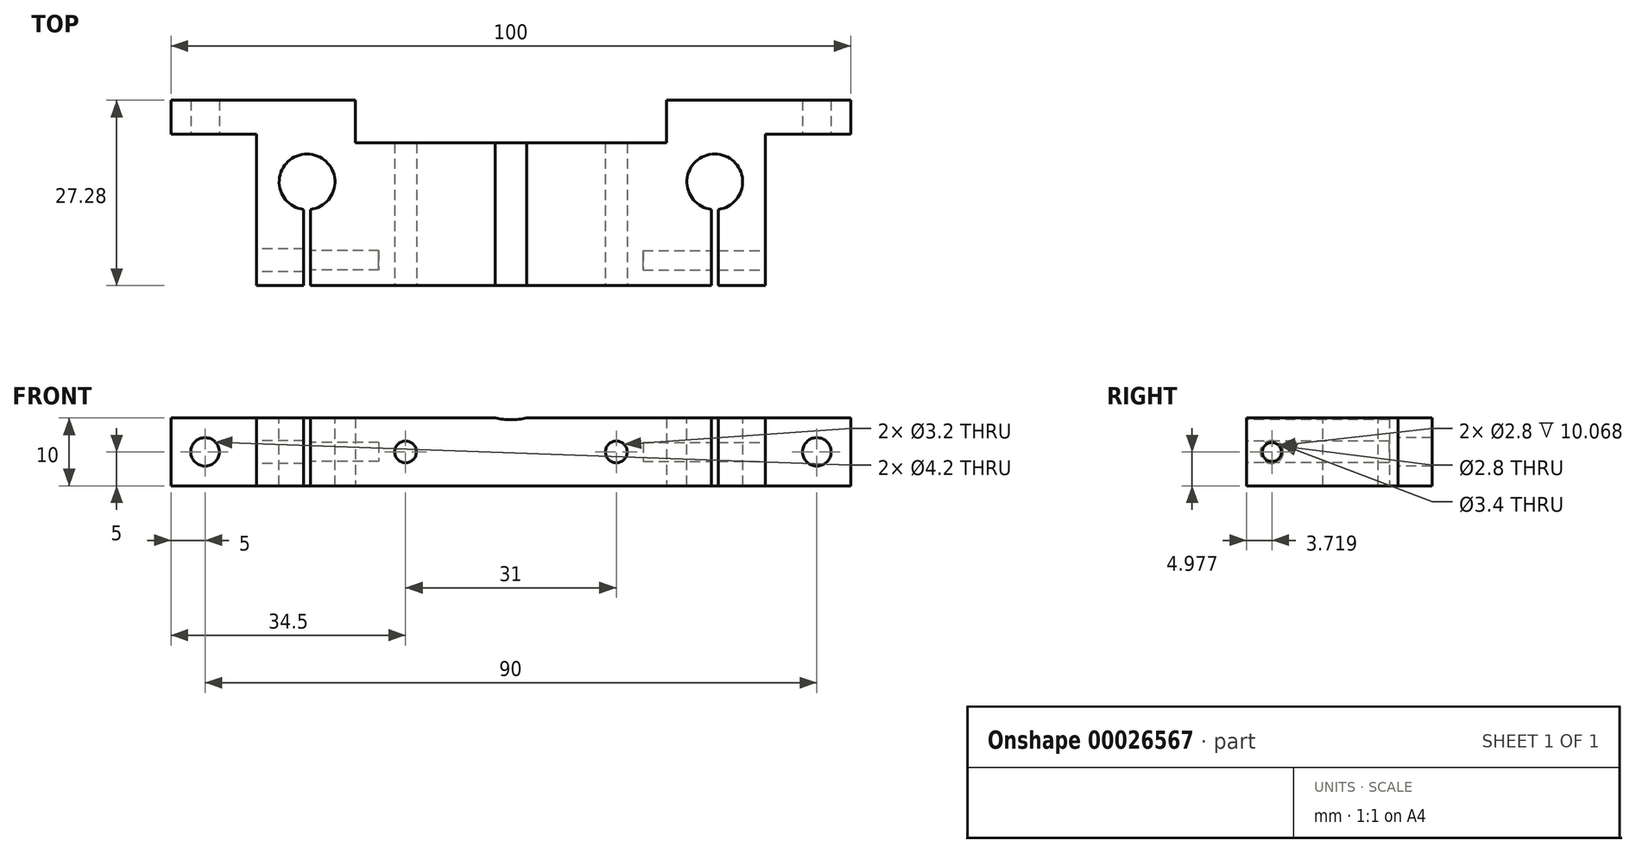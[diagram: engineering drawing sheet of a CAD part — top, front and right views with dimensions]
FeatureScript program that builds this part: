
annotation { "Feature Type Name" : "Feature", "Feature Type Description" : "" }
export const myFeature = defineFeature(function(context is Context, id is Id, definition is map)
    precondition{}
    {
        {
            var Q0;
            Q0=qCreatedBy(makeId("Top.planeOp"),FACE);
            var sketch = newSketch(context, id + "F0", { "sketchPlane" : qUnion([Q0])});
            skLineSegment(sketch, "E0", {"start": v(0, -13.82) * mm, "end": v(-37.44, -13.82) * mm});
            skLineSegment(sketch, "E1", {"start": v(-37.44, -13.82) * mm, "end": v(-37.44, 8.46) * mm});
            skLineSegment(sketch, "E2", {"start": v(-37.44, 8.46) * mm, "end": v(-50, 8.46) * mm});
            skLineSegment(sketch, "E3", {"start": v(-50, 8.46) * mm, "end": v(-50, 13.46) * mm});
            skLineSegment(sketch, "E4", {"start": v(-50, 13.46) * mm, "end": v(-22.87, 13.46) * mm});
            skLineSegment(sketch, "E5", {"start": v(-22.87, 13.46) * mm, "end": v(-22.87, 7.18) * mm});
            skLineSegment(sketch, "E6", {"start": v(-22.87, 7.18) * mm, "end": v(0, 7.18) * mm});
            skLineSegment(sketch, "E7", {"start": v(0, 7.18) * mm, "end": v(0, -13.82) * mm});
            skSolve(sketch);
        }
        {
            var Q0;
            Q0=qSketchRegion(id+"F0",true);
            extrude(context, id + "F1", {"entities" : qUnion([Q0]), "depth" : 10 * mm});
        }
        {
            var Q0;
            Q0=makeQuery(id+"F1.opExtrude","SWEPT_FACE",FACE,{"disambiguationData":[OSD([sQuery(id+"F0.wireOp",EDGE,"E0")])]});
            var sketch = newSketch(context, id + "F2", { "sketchPlane" : qUnion([Q0])});
            skLineSegment(sketch, "E8", {"start": v(0, 5) * mm, "end": v(0, 5) * mm});
            skCircle(sketch, "E9", {"center": v(-15.5, 5) * mm, "radius": 1.6 * mm});
            skCircle(sketch, "E10", {"center": v(0, 20.5) * mm, "radius": 10.75 * mm});
            skSolve(sketch);
        }
        {
            var Q0;
            Q0=qSketchRegion(id+"F2",true);
            extrude(context, id + "F3", {"entities" : qUnion([Q0]), "operationType" : NewBodyOperationType.REMOVE, "endBound" : BoundingType.THROUGH_ALL, "oppositeDirection" : true, "depth" : 25 * mm});
        }
        {
            var Q0;
            Q0=makeQuery(id+"F1.opExtrude","SWEPT_FACE",FACE,{"disambiguationData":[OSD([sQuery(id+"F0.wireOp",EDGE,"E2")])]});
            var sketch = newSketch(context, id + "F4", { "sketchPlane" : qUnion([Q0])});
            skLineSegment(sketch, "E11", {"start": v(-50, 5) * mm, "end": v(-37.44, 5) * mm, "construction": true});
            skLineSegment(sketch, "E12", {"start": v(-43.72, 10) * mm, "end": v(-43.72, 0) * mm, "construction": true});
            skCircle(sketch, "E13", {"center": v(-45, 5) * mm, "radius": 2.1 * mm});
            skSolve(sketch);
        }
        {
            var Q0;
            Q0=qSketchRegion(id+"F4",true);
            extrude(context, id + "F5", {"entities" : qUnion([Q0]), "operationType" : NewBodyOperationType.REMOVE, "endBound" : BoundingType.THROUGH_ALL, "oppositeDirection" : true, "depth" : 25 * mm});
        }
        {
            var Q0;
            {var subQ0=makeQuery(id+"F1.opExtrude","CAP_FACE",FACE,{"disambiguationData":[OSD([sQuery(id+"F0.wireOp",EDGE,"E0"),sQuery(id+"F0.wireOp",EDGE,"fd64a43a-5635-4f94-a977-4dd36923accb"),sQuery(id+"F0.wireOp",EDGE,"1334f7d4-4c90-4769-8fa3-fe5f576fb005"),sQuery(id+"F0.wireOp",EDGE,"E1"),sQuery(id+"F0.wireOp",EDGE,"E2"),sQuery(id+"F0.wireOp",EDGE,"E3"),sQuery(id+"F0.wireOp",EDGE,"E4"),sQuery(id+"F0.wireOp",EDGE,"E5"),sQuery(id+"F0.wireOp",EDGE,"E6"),sQuery(id+"F0.wireOp",EDGE,"E7")])],"isStart":false});Q0=makeQuery(id+"F10.boolean.opBoolean","MERGE",FACE,{"derivedFrom":[subQ0,makeQuery(id+"F10.opPattern","COPY",FACE,{"derivedFrom":subQ0,"instanceName":"1"})]});}
            var sketch = newSketch(context, id + "F6", { "sketchPlane" : qUnion([Q0])});
            skCircle(sketch, "E14", {"center": v(-30, 1.46) * mm, "radius": 4.1 * mm});
            skLineSegment(sketch, "E15", {"start": v(-30, 1.46) * mm, "end": v(-30, -13.82) * mm, "construction": true});
            skLineSegment(sketch, "E16.bottom", {"start": v(-30.49, -2.04) * mm, "end": v(-29.51, -2.04) * mm});
            skLineSegment(sketch, "E16.top", {"start": v(-30.49, -14.16) * mm, "end": v(-29.51, -14.16) * mm});
            skLineSegment(sketch, "E16.left", {"start": v(-30.49, -2.04) * mm, "end": v(-30.49, -14.16) * mm});
            skLineSegment(sketch, "E16.right", {"start": v(-29.51, -2.04) * mm, "end": v(-29.51, -14.16) * mm});
            skPoint(sketch, "E17", {"position": v(-30, -2.04) * mm});
            skSolve(sketch);
        }
        {
            var Q0;
            Q0=qSketchRegion(id+"F6",true);
            var Q1;
            {var subQ3=sQuery(id+"F6.wireOp",EDGE,"E16.bottom");Q1=makeQuery(id+"F6.imprint","IMPRINT",FACE,{"disambiguationData":[TD([[makeQuery(id+"F6.imprint","IMPRINT",EDGE,{"derivedFrom":subQ3}),-1.0]])]});}
            extrude(context, id + "F7", {"entities" : qUnion([Q0, Q1]), "operationType" : NewBodyOperationType.REMOVE, "endBound" : BoundingType.THROUGH_ALL, "oppositeDirection" : true, "depth" : 25 * mm});
        }
        {
            var Q0;
            Q0=makeQuery(id+"F1.opExtrude","SWEPT_FACE",FACE,{"disambiguationData":[OSD([sQuery(id+"F0.wireOp",EDGE,"E1")])]});
            var sketch = newSketch(context, id + "F8", { "sketchPlane" : qUnion([Q0])});
            skCircle(sketch, "E18", {"center": v(10.1, 4.98) * mm, "radius": 1.4 * mm});
            skCircle(sketch, "E19", {"center": v(10.1, 4.98) * mm, "radius": 1.7 * mm});
            skSolve(sketch);
        }
        {
            var Q0;
            Q0=makeQuery(id+"F8.imprint","IMPRINT",FACE,{"disambiguationData":[TD([[makeQuery(id+"F8.imprint","IMPRINT",EDGE,{"derivedFrom":sQuery(id+"F8.wireOp",EDGE,"E18")}),1.0]])]});
            extrude(context, id + "F9", {"entities" : qUnion([Q0]), "operationType" : NewBodyOperationType.REMOVE, "oppositeDirection" : true, "depth" : 18 * mm});
        }
        {
            var Q0;
            Q0=makeQuery(id+"F1.opExtrude","SWEPT_BODY",BODY,{"disambiguationData":[OSD([sQuery(id+"F0.wireOp",EDGE,"E0"),sQuery(id+"F0.wireOp",EDGE,"fd64a43a-5635-4f94-a977-4dd36923accb"),sQuery(id+"F0.wireOp",EDGE,"1334f7d4-4c90-4769-8fa3-fe5f576fb005"),sQuery(id+"F0.wireOp",EDGE,"E1"),sQuery(id+"F0.wireOp",EDGE,"E2"),sQuery(id+"F0.wireOp",EDGE,"E3"),sQuery(id+"F0.wireOp",EDGE,"E4"),sQuery(id+"F0.wireOp",EDGE,"E5"),sQuery(id+"F0.wireOp",EDGE,"E6"),sQuery(id+"F0.wireOp",EDGE,"E7")])]});
            var Q1;
            Q1=qCreatedBy(makeId("Right.planeOp"),FACE);
            mirror(context, id + "F10", {"operationType" : NewBodyOperationType.ADD, "entities" : qUnion([Q0]), "mirrorPlane" : qUnion([Q1])});
        }
        {
            var Q0;
            Q0=makeQuery(id+"F8.imprint","IMPRINT",FACE,{"disambiguationData":[TD([[makeQuery(id+"F8.imprint","IMPRINT",EDGE,{"derivedFrom":sQuery(id+"F8.wireOp",EDGE,"E18")}),1.0]])]});
            var Q1;
            Q1=makeQuery(id+"F8.imprint","IMPRINT",FACE,{"disambiguationData":[TD([[makeQuery(id+"F8.imprint","IMPRINT",EDGE,{"derivedFrom":sQuery(id+"F8.wireOp",EDGE,"E18")}),-1.0]])]});
            extrude(context, id + "F11", {"entities" : qUnion([Q0, Q1]), "operationType" : NewBodyOperationType.REMOVE, "endBound" : BoundingType.UP_TO_NEXT, "oppositeDirection" : true, "depth" : 25 * mm});
        }
    });
